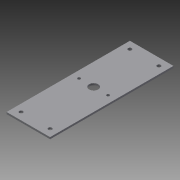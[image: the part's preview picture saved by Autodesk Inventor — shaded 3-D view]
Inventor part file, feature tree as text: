
AUTODESK INVENTOR PART (.ipt)
format: ipt  version: 2015 SP1 (Build 190203100, 203)  size: 102,912 bytes
history: native  units: in
note: dims shown in document units (in); Inventor stores cm internally (conversion verified against a paired STEP export)
features: sketch x3, extrude x2, hole x1
ambient origin geometry x8: Origin, YZ Plane, XZ Plane, XY Plane, X Axis, Y Axis, Z Axis, Center Point
bodies: Solid1 (feature_tree)
feature tree (6):
  extrude  "Extrusion1"  Depth=8.5in
  extrude  "Extrusion2"  Depth=0.125in
  hole  "Hole1"  [1 undecoded]
  sketch  "Sketch1"  dims[d0=3.0in d1=8.5in]
  sketch  "Sketch2"  dims[d2=0.125in d3=0.0in d4=4.25in]
  sketch  "Sketch3"  dims[d5=1.5in d6=1.0in d7=1.0in d8=4.25in d9=4.25in d10=0.2in d11=0.2in d12=0.625in d13=1.0in d14=0.0in d15=0.5in d16=0.5in d17=0.5in d18=0.5in d19=0.5in d20=0.5in d21=0.5in d22=0.5in d23=0.25in d24=0.75in d25=0.375in d26=0.25in d27=0.5635in d28=1.0in d29=0.8108in]
note: 1 required parameter value undecoded (feature->parameter linkage not recoverable at this tier; creation-order binding heuristic only, values carry confidence <= 0.55)
